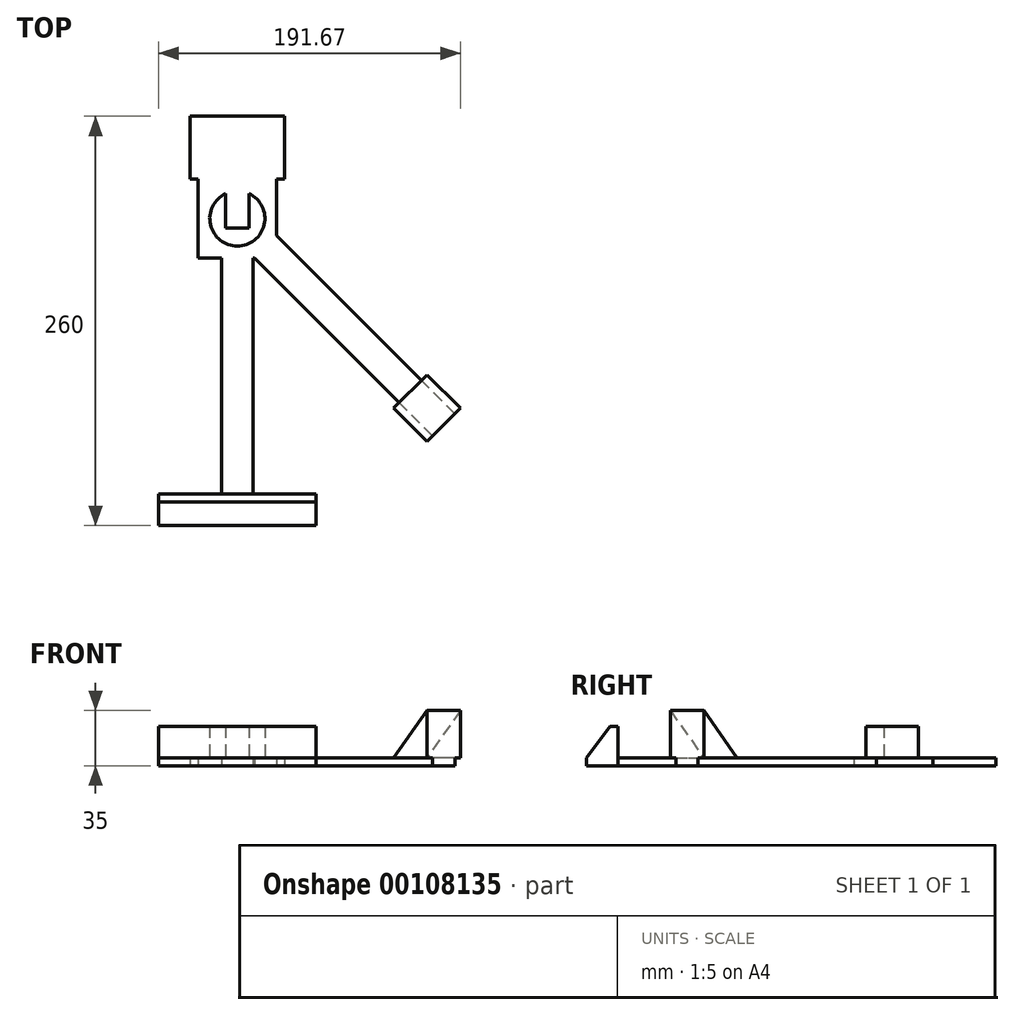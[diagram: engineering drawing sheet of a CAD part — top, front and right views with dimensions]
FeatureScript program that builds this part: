
annotation { "Feature Type Name" : "Feature", "Feature Type Description" : "" }
export const myFeature = defineFeature(function(context is Context, id is Id, definition is map)
    precondition{}
    {
        {
            var Q0;
            Q0=qCreatedBy(makeId("Top.planeOp"),FACE);
            var sketch = newSketch(context, id + "F0", { "sketchPlane" : qUnion([Q0])});
            skLineSegment(sketch, "E0.bottom", {"start": v(-87.86, -3.02) * mm, "end": v(-37.86, -3.02) * mm});
            skLineSegment(sketch, "E0.top", {"start": v(-87.86, -53.02) * mm, "end": v(-37.86, -53.02) * mm});
            skLineSegment(sketch, "E0.left", {"start": v(-87.86, -3.02) * mm, "end": v(-87.86, -53.02) * mm});
            skLineSegment(sketch, "E0.right", {"start": v(-37.86, -3.02) * mm, "end": v(-37.86, -53.02) * mm});
            skLineSegment(sketch, "E1.bottom", {"start": v(-72.86, -53.02) * mm, "end": v(-52.86, -53.02) * mm});
            skLineSegment(sketch, "E1.top", {"start": v(-72.86, -203.02) * mm, "end": v(-52.86, -203.02) * mm});
            skLineSegment(sketch, "E1.left", {"start": v(-72.86, -53.02) * mm, "end": v(-72.86, -203.02) * mm});
            skLineSegment(sketch, "E1.right", {"start": v(-52.86, -53.02) * mm, "end": v(-52.86, -203.02) * mm});
            skLineSegment(sketch, "E2.bottom", {"start": v(-112.86, -203.02) * mm, "end": v(-12.86, -203.02) * mm});
            skLineSegment(sketch, "E2.top", {"start": v(-112.86, -223.02) * mm, "end": v(-12.86, -223.02) * mm});
            skLineSegment(sketch, "E2.left", {"start": v(-112.86, -203.02) * mm, "end": v(-112.86, -223.02) * mm});
            skLineSegment(sketch, "E2.right", {"start": v(-12.86, -203.02) * mm, "end": v(-12.86, -223.02) * mm});
            skLineSegment(sketch, "E3.bottom", {"start": v(61.13, -166.16) * mm, "end": v(-52, -53.02) * mm});
            skLineSegment(sketch, "E3.top", {"start": v(75.27, -152.02) * mm, "end": v(-37.86, -38.88) * mm});
            skLineSegment(sketch, "E3.left", {"start": v(61.13, -166.16) * mm, "end": v(75.27, -152.02) * mm});
            skPoint(sketch, "E3.middle", {"position": v(-37.86, -53.02) * mm});
            skLineSegment(sketch, "E4", {"start": v(-52, -53.02) * mm, "end": v(-37.86, -38.88) * mm});
            skPoint(sketch, "E5.orphan", {"position": v(-136.86, 60.11) * mm});
            skPoint(sketch, "E6.orphan", {"position": v(-151, 45.97) * mm});
            skLineSegment(sketch, "E7", {"start": v(-62.86, -203.02) * mm, "end": v(-62.86, -53.02) * mm});
            skCircle(sketch, "E8", {"center": v(-62.86, -28.02) * mm, "radius": 17.5 * mm});
            skPoint(sketch, "E8.centerSnap0", {"position": v(-87.86, -28.02) * mm});
            skPoint(sketch, "E8.centerSnap1", {"position": v(-62.86, -3.02) * mm});
            skLineSegment(sketch, "E9.bottom", {"start": v(-32.86, -3.02) * mm, "end": v(-92.86, -3.02) * mm});
            skLineSegment(sketch, "E9.top", {"start": v(-32.86, 36.98) * mm, "end": v(-92.86, 36.98) * mm});
            skLineSegment(sketch, "E9.left", {"start": v(-32.86, -3.02) * mm, "end": v(-32.86, 36.98) * mm});
            skLineSegment(sketch, "E9.right", {"start": v(-92.86, -3.02) * mm, "end": v(-92.86, 36.98) * mm});
            skLineSegment(sketch, "E10.bottom", {"start": v(-70.36, -34.02) * mm, "end": v(-55.36, -34.02) * mm});
            skLineSegment(sketch, "E10.top", {"start": v(-70.36, 27.98) * mm, "end": v(-55.36, 27.98) * mm});
            skLineSegment(sketch, "E10.left", {"start": v(-70.36, -34.02) * mm, "end": v(-70.36, 27.98) * mm});
            skLineSegment(sketch, "E10.right", {"start": v(-55.36, -34.02) * mm, "end": v(-55.36, 27.98) * mm});
            skSolve(sketch);
        }
        {
            var Q0;
            {var subQ1=sQuery(id+"F0.wireOp",EDGE,"E0.bottom");Q0=makeQuery(id+"F0.imprint","IMPRINT",FACE,{"disambiguationData":[TD([[makeQuery(id+"F0.imprint","IMPRINT",EDGE,{"derivedFrom":subQ1}),-1.0]])]});}
            var Q1;
            {var subQ0=sQuery(id+"F0.wireOp",EDGE,"E1.left");Q1=makeQuery(id+"F0.imprint","IMPRINT",FACE,{"disambiguationData":[TD([[makeQuery(id+"F0.imprint","IMPRINT",EDGE,{"derivedFrom":subQ0}),1.0]])]});}
            var Q2;
            {var subQ3=sQuery(id+"F0.wireOp",EDGE,"E7");Q2=makeQuery(id+"F0.imprint","IMPRINT",FACE,{"disambiguationData":[TD([[makeQuery(id+"F0.imprint","IMPRINT",EDGE,{"derivedFrom":subQ3}),-1.0]])]});}
            var Q3;
            {var subQ5=sQuery(id+"F0.wireOp",EDGE,"E4");Q3=makeQuery(id+"F0.imprint","IMPRINT",FACE,{"disambiguationData":[TD([[makeQuery(id+"F0.imprint","IMPRINT",EDGE,{"derivedFrom":subQ5}),-1.0]])]});}
            var Q4;
            {var subQ0=sQuery(id+"F0.wireOp",EDGE,"E1.right");var subQ3=sQuery(id+"F0.wireOp",EDGE,"E3.bottom");var subQ5=makeQuery(id+"F0.imprint","INTERSECT",VERTEX,{"derivedFrom":[subQ0,subQ3]});Q4=makeQuery(id+"F0.imprint","IMPRINT",FACE,{"disambiguationData":[TD([[makeQuery(id+"F0.imprint","IMPRINT",EDGE,{"disambiguationData":[TD([[subQ5,1.0]])],"derivedFrom":subQ0}),-1.0]])]});}
            var Q5;
            {var subQ8=sQuery(id+"F0.wireOp",EDGE,"E3.top");Q5=makeQuery(id+"F0.imprint","IMPRINT",FACE,{"disambiguationData":[TD([[makeQuery(id+"F0.imprint","IMPRINT",EDGE,{"derivedFrom":subQ8}),1.0]])]});}
            var Q6;
            {var subQ4=sQuery(id+"F0.wireOp",EDGE,"E0.left");Q6=makeQuery(id+"F0.imprint","IMPRINT",FACE,{"disambiguationData":[TD([[makeQuery(id+"F0.imprint","IMPRINT",EDGE,{"derivedFrom":subQ4}),1.0]])]});}
            var Q7;
            Q7=makeQuery(id+"F0.imprint","IMPRINT",FACE,{"disambiguationData":[TD([[makeQuery(id+"F0.imprint","IMPRINT",EDGE,{"derivedFrom":sQuery(id+"F0.wireOp",EDGE,"E9.top")}),1.0]])]});
            var Q8;
            {var subQ5=sQuery(id+"F0.wireOp",EDGE,"E10.top");Q8=makeQuery(id+"F0.imprint","IMPRINT",FACE,{"disambiguationData":[TD([[makeQuery(id+"F0.imprint","IMPRINT",EDGE,{"derivedFrom":subQ5}),-1.0]])]});}
            var Q9;
            {var subQ0=sQuery(id+"F0.wireOp",EDGE,"E10.left");var subQ1=sQuery(id+"F0.wireOp",EDGE,"E8");var subQ2=makeQuery(id+"F0.imprint","INTERSECT",VERTEX,{"derivedFrom":[subQ1,subQ0]});Q9=makeQuery(id+"F0.imprint","IMPRINT",FACE,{"disambiguationData":[TD([[makeQuery(id+"F0.imprint","IMPRINT",EDGE,{"disambiguationData":[TD([[subQ2,1.0]])],"derivedFrom":subQ1}),-1.0]])]});}
            var Q10;
            {var subQ5=sQuery(id+"F0.wireOp",EDGE,"E10.bottom");Q10=makeQuery(id+"F0.imprint","IMPRINT",FACE,{"disambiguationData":[TD([[makeQuery(id+"F0.imprint","IMPRINT",EDGE,{"derivedFrom":subQ5}),1.0]])]});}
            extrude(context, id + "F1", {"entities" : qUnion([Q0, Q1, Q2, Q3, Q4, Q5, Q6, Q7, Q8, Q9, Q10]), "depth" : 5 * mm});
        }
        {
            var Q0;
            {var subQ5=sQuery(id+"F0.wireOp",EDGE,"E10.bottom");Q0=makeQuery(id+"F0.imprint","IMPRINT",FACE,{"disambiguationData":[TD([[makeQuery(id+"F0.imprint","IMPRINT",EDGE,{"derivedFrom":subQ5}),-1.0]])]});}
            extrude(context, id + "F2", {"entities" : qUnion([Q0]), "operationType" : NewBodyOperationType.ADD, "depth" : 25 * mm});
        }
        {
            var Q0;
            Q0=makeQuery(id+"F0.imprint","IMPRINT",FACE,{"disambiguationData":[TD([[makeQuery(id+"F0.imprint","IMPRINT",EDGE,{"derivedFrom":sQuery(id+"F0.wireOp",EDGE,"E2.top")}),1.0]])]});
            extrude(context, id + "F3", {"entities" : qUnion([Q0]), "operationType" : NewBodyOperationType.ADD, "depth" : 25 * mm});
        }
        {
            var Q0;
            Q0=makeQuery(id+"F1.opExtrude","SWEPT_FACE",FACE,{"disambiguationData":[OSD([sQuery(id+"F0.wireOp",EDGE,"E3.top")])]});
            var sketch = newSketch(context, id + "F4", { "sketchPlane" : qUnion([Q0])});
            skLineSegment(sketch, "E11", {"start": v(-160.72, 0) * mm, "end": v(-160.72, 35) * mm});
            skLineSegment(sketch, "E12", {"start": v(-160.72, 35) * mm, "end": v(-130.72, 5) * mm});
            skLineSegment(sketch, "E13", {"start": v(-130.72, 5) * mm, "end": v(-160.72, 5) * mm});
            skSolve(sketch);
        }
        {
            var Q0;
            {var subQ2=sQuery(id+"F4.wireOp",EDGE,"E12");Q0=makeQuery(id+"F4.imprint","IMPRINT",FACE,{"disambiguationData":[TD([[makeQuery(id+"F4.imprint","IMPRINT",EDGE,{"derivedFrom":subQ2}),-1.0]])]});}
            var Q1;
            Q1 = qSketchRegion(id + "F4", true);
            extrude(context, id + "F5", {"entities" : qUnion([Q0, Q1]), "operationType" : NewBodyOperationType.ADD, "oppositeDirection" : true, "depth" : 25 * mm, "hasSecondDirection" : true, "secondDirectionOppositeDirection" : false, "secondDirectionDepth" : 5 * mm});
        }
        {
            var Q0;
            Q0=makeQuery(id+"F3.opExtrude","SWEPT_FACE",FACE,{"disambiguationData":[OSD([sQuery(id+"F0.wireOp",EDGE,"E2.left")])]});
            var sketch = newSketch(context, id + "F6", { "sketchPlane" : qUnion([Q0])});
            skLineSegment(sketch, "E14", {"start": v(208.02, 25) * mm, "end": v(223.02, 5) * mm});
            skSolve(sketch);
        }
        {
            var Q0;
            {var subQ0=sQuery(id+"F6.wireOp",EDGE,"E14");Q0=makeQuery(id+"F6.imprint","IMPRINT",FACE,{"disambiguationData":[TD([[makeQuery(id+"F6.imprint","IMPRINT",EDGE,{"derivedFrom":subQ0}),1.0]])]});}
            var Q1;
            Q1=makeQuery(id+"F3.opExtrude","SWEPT_FACE",FACE,{"disambiguationData":[OSD([sQuery(id+"F0.wireOp",EDGE,"E2.right")])]});
            extrude(context, id + "F7", {"entities" : qUnion([Q0]), "operationType" : NewBodyOperationType.REMOVE, "endBound" : BoundingType.UP_TO_SURFACE, "oppositeDirection" : true, "endBoundEntityFace" : qUnion([Q1]), "depth" : 25 * mm});
        }
    });
